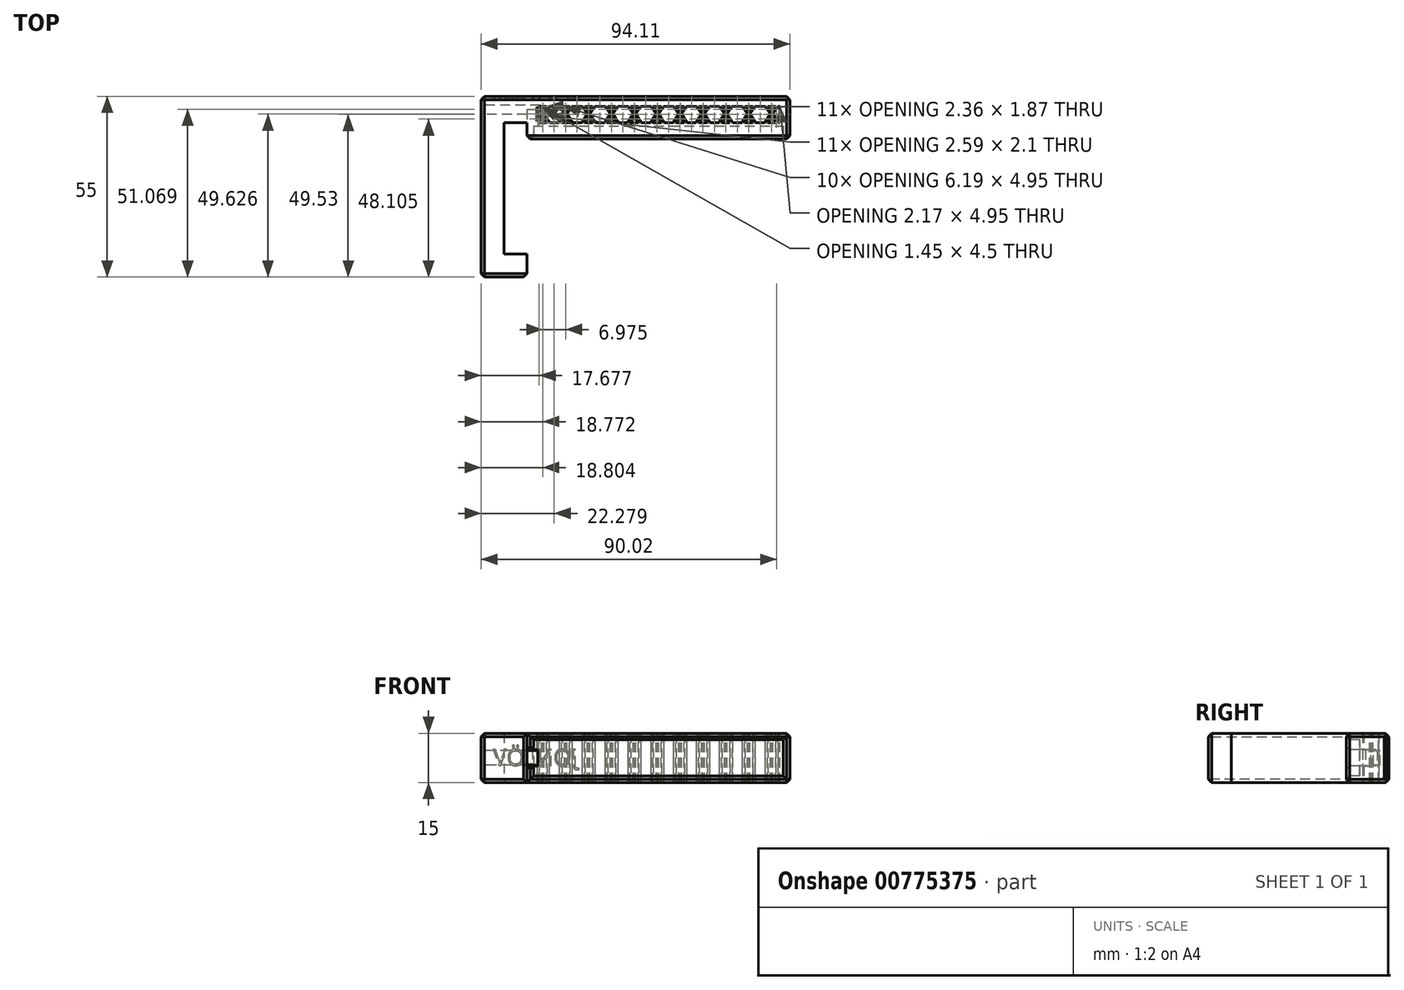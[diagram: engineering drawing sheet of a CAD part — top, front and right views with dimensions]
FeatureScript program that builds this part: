
annotation { "Feature Type Name" : "Feature", "Feature Type Description" : "" }
export const myFeature = defineFeature(function(context is Context, id is Id, definition is map)
    precondition{}
    {
        {
            var Q0;
            Q0=qCreatedBy(makeId("Top.planeOp"),FACE);
            var sketch = newSketch(context, id + "F0", { "sketchPlane" : qUnion([Q0])});
            skLineSegment(sketch, "E0", {"start": v(-19.56, 42.56) * mm, "end": v(-19.56, -12.44) * mm});
            skLineSegment(sketch, "E1", {"start": v(-19.56, -12.44) * mm, "end": v(-5.6, -12.44) * mm});
            skLineSegment(sketch, "E2", {"start": v(-5.6, -12.44) * mm, "end": v(-5.6, -5.44) * mm});
            skLineSegment(sketch, "E3", {"start": v(-5.6, -5.44) * mm, "end": v(-12.56, -5.44) * mm});
            skLineSegment(sketch, "E4", {"start": v(-12.56, -5.44) * mm, "end": v(-12.56, 34.61) * mm});
            skLineSegment(sketch, "E5", {"start": v(-12.56, 34.61) * mm, "end": v(-5.6, 34.61) * mm});
            skLineSegment(sketch, "E6", {"start": v(-5.6, 34.61) * mm, "end": v(-5.6, 29.61) * mm});
            skLineSegment(sketch, "E7", {"start": v(-19.56, 42.56) * mm, "end": v(74.55, 42.56) * mm});
            skLineSegment(sketch, "E8", {"start": v(-5.6, 29.61) * mm, "end": v(74.55, 29.61) * mm});
            skLineSegment(sketch, "E9", {"start": v(74.55, 29.61) * mm, "end": v(74.55, 42.56) * mm});
            skSolve(sketch);
        }
        {
            var Q0;
            Q0=makeQuery(id+"F0.imprint","IMPRINT",FACE,{"disambiguationData":[TD([[makeQuery(id+"F0.imprint","IMPRINT",EDGE,{"derivedFrom":sQuery(id+"F0.wireOp",EDGE,"E0")}),1.0]])]});
            extrude(context, id + "F1", {"entities" : qUnion([Q0]), "depth" : 15 * mm, "offsetDistance" : 25 * mm});
        }
        {
            var Q0;
            Q0=makeQuery(id+"F1.opExtrude","CAP_FACE",FACE,{"disambiguationData":[OSD([sQuery(id+"F0.wireOp",EDGE,"E0"),sQuery(id+"F0.wireOp",EDGE,"E1"),sQuery(id+"F0.wireOp",EDGE,"E2"),sQuery(id+"F0.wireOp",EDGE,"E3"),sQuery(id+"F0.wireOp",EDGE,"E4"),sQuery(id+"F0.wireOp",EDGE,"E5"),sQuery(id+"F0.wireOp",EDGE,"E6"),sQuery(id+"F0.wireOp",EDGE,"E7"),sQuery(id+"F0.wireOp",EDGE,"E8"),sQuery(id+"F0.wireOp",EDGE,"E9")])],"isStart":false});
            var sketch = newSketch(context, id + "F2", { "sketchPlane" : qUnion([Q0])});
            skLineSegment(sketch, "E10", {"start": v(-5.6, 34.61) * mm, "end": v(-5.6, 42.56) * mm, "construction": true});
            skLineSegment(sketch, "E11", {"start": v(74.55, 42.56) * mm, "end": v(74.55, 29.61) * mm, "construction": true});
            skLineSegment(sketch, "E12", {"start": v(74.55, 29.61) * mm, "end": v(-5.6, 29.61) * mm, "construction": true});
            skLineSegment(sketch, "E13", {"start": v(-5.6, 29.61) * mm, "end": v(-5.6, 34.61) * mm, "construction": true});
            skLineSegment(sketch, "E14.0", {"start": v(-2.6, 39.56) * mm, "end": v(71.55, 39.56) * mm});
            skLineSegment(sketch, "E14.1", {"start": v(-2.6, 34.61) * mm, "end": v(-2.6, 39.56) * mm});
            skLineSegment(sketch, "E14.2", {"start": v(71.55, 34.61) * mm, "end": v(-2.6, 34.61) * mm});
            skLineSegment(sketch, "E14.3", {"start": v(71.55, 39.56) * mm, "end": v(71.55, 34.61) * mm});
            skSolve(sketch);
        }
        {
            var Q0;
            Q0=makeQuery(id+"F2.imprint","IMPRINT",FACE,{"disambiguationData":[TD([[makeQuery(id+"F2.imprint","IMPRINT",EDGE,{"derivedFrom":sQuery(id+"F2.wireOp",EDGE,"E14.0")}),-1.0]])]});
            extrude(context, id + "F3", {"entities" : qUnion([Q0]), "operationType" : NewBodyOperationType.REMOVE, "endBound" : BoundingType.THROUGH_ALL, "oppositeDirection" : true, "depth" : 25 * mm, "offsetDistance" : 25 * mm});
        }
        {
            var Q0;
            Q0=makeQuery(id+"F1.opExtrude","CAP_FACE",FACE,{"disambiguationData":[OSD([sQuery(id+"F0.wireOp",EDGE,"E0"),sQuery(id+"F0.wireOp",EDGE,"E1"),sQuery(id+"F0.wireOp",EDGE,"E2"),sQuery(id+"F0.wireOp",EDGE,"E3"),sQuery(id+"F0.wireOp",EDGE,"E4"),sQuery(id+"F0.wireOp",EDGE,"E5"),sQuery(id+"F0.wireOp",EDGE,"E6"),sQuery(id+"F0.wireOp",EDGE,"E7"),sQuery(id+"F0.wireOp",EDGE,"E8"),sQuery(id+"F0.wireOp",EDGE,"E9")])],"isStart":false});
            var sketch = newSketch(context, id + "F4", { "sketchPlane" : qUnion([Q0])});
            skSolve(sketch);
        }
        {
            var Q0;
            Q0=makeQuery(id+"F4.imprint","IMPRINT",FACE,{"disambiguationData":[TD([[makeQuery(id+"F4.imprint","IMPRINT",EDGE,{"derivedFrom":makeQuery(id+"F1.opExtrude","CAP_EDGE",EDGE,{"disambiguationData":[OSD([sQuery(id+"F0.wireOp",EDGE,"E0")])],"isStart":false})}),1.0]])]});
            var sketch = newSketch(context, id + "F5", { "sketchPlane" : qUnion([Q0])});
            skText(sketch, "E15", { "text": "X X X X X X X X X X X", "fontName": "OpenSans-Regular.ttf"});
            const initialGuessF5  = {"E15": [-0.00317, 0.0341, 1, 0, 0.006]};
            skSetInitialGuess(sketch, initialGuessF5);
            skSolve(sketch);
        }
        {
            var Q0;
            Q0 = qSketchRegion(id + "F5", true);
            extrude(context, id + "F6", {"entities" : qUnion([Q0]), "operationType" : NewBodyOperationType.ADD, "oppositeDirection" : true, "depth" : 15 * mm, "offsetDistance" : 25 * mm});
        }
        {
            var Q0;
            Q0=makeQuery(id+"F1.opExtrude","SWEPT_EDGE",EDGE,{"disambiguationData":[OSD([sQuery(id+"F0.wireOp",EDGE,"E7"),sQuery(id+"F0.wireOp",EDGE,"E9")])]});
            var Q1;
            Q1=makeQuery(id+"F1.opExtrude","SWEPT_EDGE",EDGE,{"disambiguationData":[OSD([sQuery(id+"F0.wireOp",EDGE,"E0"),sQuery(id+"F0.wireOp",EDGE,"E7")])]});
            var Q2;
            Q2=makeQuery(id+"F1.opExtrude","SWEPT_EDGE",EDGE,{"disambiguationData":[OSD([sQuery(id+"F0.wireOp",EDGE,"E0"),sQuery(id+"F0.wireOp",EDGE,"E1")])]});
            var Q3;
            Q3=makeQuery(id+"F1.opExtrude","SWEPT_FACE",FACE,{"disambiguationData":[OSD([sQuery(id+"F0.wireOp",EDGE,"E7")])]});
            var Q4;
            Q4=makeQuery(id+"F1.opExtrude","SWEPT_FACE",FACE,{"disambiguationData":[OSD([sQuery(id+"F0.wireOp",EDGE,"E0")])]});
            var Q5;
            Q5=makeQuery(id+"F1.opExtrude","SWEPT_FACE",FACE,{"disambiguationData":[OSD([sQuery(id+"F0.wireOp",EDGE,"E1")])]});
            chamfer(context, id + "F7", {"entities" : qUnion([Q0, Q1, Q2, Q3, Q4, Q5]), "width" : 1 * mm, "tangentPropagation" : true});
        }
        {
            var Q0;
            Q0=makeQuery(id+"F1.opExtrude","SWEPT_FACE",FACE,{"disambiguationData":[OSD([sQuery(id+"F0.wireOp",EDGE,"E8")])]});
            var sketch = newSketch(context, id + "F8", { "sketchPlane" : qUnion([Q0])});
            skLineSegment(sketch, "E16.0", {"start": v(-3.6, 2) * mm, "end": v(72.55, 2) * mm});
            skLineSegment(sketch, "E16.1", {"start": v(-3.6, 13) * mm, "end": v(-3.6, 2) * mm});
            skLineSegment(sketch, "E16.2", {"start": v(72.55, 13) * mm, "end": v(-3.6, 13) * mm});
            skLineSegment(sketch, "E16.3", {"start": v(72.55, 2) * mm, "end": v(72.55, 13) * mm});
            skSolve(sketch);
        }
        {
            var Q0;
            Q0=makeQuery(id+"F8.imprint","IMPRINT",FACE,{"disambiguationData":[TD([[makeQuery(id+"F8.imprint","IMPRINT",EDGE,{"derivedFrom":sQuery(id+"F8.wireOp",EDGE,"E16.0")}),1.0]])]});
            extrude(context, id + "F9", {"entities" : qUnion([Q0]), "operationType" : NewBodyOperationType.REMOVE, "oppositeDirection" : true, "depth" : 4 * mm, "offsetDistance" : 25 * mm});
        }
        {
            var Q0;
            Q0=makeQuery(id+"F9.boolean.opBoolean","COPY",FACE,{"derivedFrom":makeQuery(id+"F9.opExtrude","SWEPT_FACE",FACE,{"disambiguationData":[OSD([sQuery(id+"F8.wireOp",EDGE,"E16.1")])]})});
            var sketch = newSketch(context, id + "F10", { "sketchPlane" : qUnion([Q0])});
            skLineSegment(sketch, "E17.bottom", {"start": v(33.61, 5) * mm, "end": v(29.61, 5) * mm});
            skLineSegment(sketch, "E17.top", {"start": v(33.61, 10) * mm, "end": v(29.61, 10) * mm});
            skLineSegment(sketch, "E17.left", {"start": v(33.61, 5) * mm, "end": v(33.61, 10) * mm});
            skLineSegment(sketch, "E17.right", {"start": v(29.61, 5) * mm, "end": v(29.61, 10) * mm});
            skSolve(sketch);
        }
        {
            var Q0;
            Q0=makeQuery(id+"F10.imprint","IMPRINT",FACE,{"disambiguationData":[TD([[makeQuery(id+"F10.imprint","IMPRINT",EDGE,{"derivedFrom":sQuery(id+"F10.wireOp",EDGE,"E17.bottom")}),-1.0]])]});
            extrude(context, id + "F11", {"entities" : qUnion([Q0]), "operationType" : NewBodyOperationType.REMOVE, "oppositeDirection" : true, "depth" : 3 * mm, "offsetDistance" : 25 * mm});
        }
        {
            var Q0;
            Q0=makeQuery(id+"F1.opExtrude","SWEPT_FACE",FACE,{"disambiguationData":[OSD([sQuery(id+"F0.wireOp",EDGE,"E0")])]});
            var sketch = newSketch(context, id + "F12", { "sketchPlane" : qUnion([Q0])});
            skLineSegment(sketch, "E18.bottom", {"start": v(-37.06, 5.3) * mm, "end": v(-39.9, 5.3) * mm});
            skLineSegment(sketch, "E18.top", {"start": v(-37.06, 9.7) * mm, "end": v(-39.9, 9.7) * mm});
            skLineSegment(sketch, "E18.left", {"start": v(-37.06, 5.3) * mm, "end": v(-37.06, 9.7) * mm});
            skLineSegment(sketch, "E18.right", {"start": v(-39.9, 5.3) * mm, "end": v(-39.9, 9.7) * mm});
            skPoint(sketch, "E18.middle", {"position": v(-38.48, 7.5) * mm});
            skPoint(sketch, "E18.middle.positionSnap0", {"position": v(-41.56, 7.5) * mm});
            skPoint(sketch, "E18.centerSnap0", {"position": v(-41.56, 7.5) * mm});
            skSolve(sketch);
        }
        {
            var Q0;
            Q0=makeQuery(id+"F12.imprint","IMPRINT",FACE,{"disambiguationData":[TD([[makeQuery(id+"F12.imprint","IMPRINT",EDGE,{"derivedFrom":sQuery(id+"F12.wireOp",EDGE,"E18.bottom")}),-1.0]])]});
            extrude(context, id + "F13", {"entities" : qUnion([Q0]), "operationType" : NewBodyOperationType.REMOVE, "oppositeDirection" : true, "depth" : 18 * mm, "offsetDistance" : 25 * mm});
        }
        {
            var Q0;
            Q0=makeQuery(id+"F11.boolean.opBoolean","MERGE",FACE,{"derivedFrom":[makeQuery(id+"F9.boolean.opBoolean","COPY",FACE,{"derivedFrom":makeQuery(id+"F9.opExtrude","CAP_FACE",FACE,{"disambiguationData":[OSD([sQuery(id+"F8.wireOp",EDGE,"E16.0"),sQuery(id+"F8.wireOp",EDGE,"E16.1"),sQuery(id+"F8.wireOp",EDGE,"E16.2"),sQuery(id+"F8.wireOp",EDGE,"E16.3")])],"isStart":false})}),makeQuery(id+"F11.opExtrude","SWEPT_FACE",FACE,{"disambiguationData":[OSD([sQuery(id+"F10.wireOp",EDGE,"E17.left")])]})]});
            var sketch = newSketch(context, id + "F14", { "sketchPlane" : qUnion([Q0])});
            skLineSegment(sketch, "E19.bottom", {"start": v(-5.6, 10) * mm, "end": v(-2.3, 10) * mm});
            skLineSegment(sketch, "E19.top", {"start": v(-5.6, 5) * mm, "end": v(-2.3, 5) * mm});
            skLineSegment(sketch, "E19.left", {"start": v(-5.6, 10) * mm, "end": v(-5.6, 5) * mm});
            skLineSegment(sketch, "E19.right", {"start": v(-2.3, 10) * mm, "end": v(-2.3, 5) * mm});
            skSolve(sketch);
        }
        {
            var Q0;
            {var subQ9=sQuery(id+"F14.wireOp",EDGE,"E19.left");Q0=makeQuery(id+"F14.imprint","IMPRINT",FACE,{"disambiguationData":[TD([[makeQuery(id+"F14.imprint","IMPRINT",EDGE,{"derivedFrom":subQ9}),1.0]])]});}
            extrude(context, id + "F15", {"entities" : qUnion([Q0]), "operationType" : NewBodyOperationType.REMOVE, "oppositeDirection" : true, "depth" : 5 * mm, "offsetDistance" : 25 * mm});
        }
        {
            var Q0;
            Q0=makeQuery(id+"F1.opExtrude","SWEPT_FACE",FACE,{"disambiguationData":[OSD([sQuery(id+"F0.wireOp",EDGE,"E9")])]});
            var Q1;
            Q1=makeQuery(id+"F1.opExtrude","SWEPT_FACE",FACE,{"disambiguationData":[OSD([sQuery(id+"F0.wireOp",EDGE,"E8")])]});
            chamfer(context, id + "F16", {"entities" : qUnion([Q0, Q1]), "width" : 1 * mm, "tangentPropagation" : true});
        }
        {
            var Q0;
            Q0=makeQuery(id+"F1.opExtrude","SWEPT_FACE",FACE,{"disambiguationData":[OSD([sQuery(id+"F0.wireOp",EDGE,"E7")])]});
            var sketch = newSketch(context, id + "F17", { "sketchPlane" : qUnion([Q0])});
            skText(sketch, "E20", { "text": "JONLÖV", "fontName": "OpenSans-Regular.ttf"});
            const initialGuessF17  = {"E20": [-0.00975, 0.00516, 1, 0, 0.005]};
            skSetInitialGuess(sketch, initialGuessF17);
            skSolve(sketch);
        }
        {
            var Q0;
            Q0 = qSketchRegion(id + "F17", true);
            extrude(context, id + "F18", {"entities" : qUnion([Q0]), "operationType" : NewBodyOperationType.REMOVE, "oppositeDirection" : true, "depth" : 1 * mm, "offsetDistance" : 25 * mm});
        }
    });
